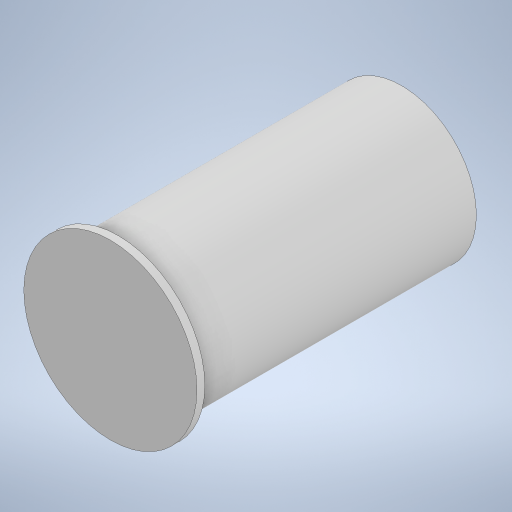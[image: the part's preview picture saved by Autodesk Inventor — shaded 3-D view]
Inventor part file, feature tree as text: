
AUTODESK INVENTOR PART (.ipt)
format: ipt  version: 2024.2 (Build 282272000, 272)  size: 210,944 bytes
history: native  units: mm
features: extrude x2, sketch x2
ambient origin geometry x8: Origin, YZ Plane, XZ Plane, XY Plane, X Axis, Y Axis, Z Axis, Center Point
bodies: Solid1 (feature_tree)
feature tree (4):
  extrude  "Extrusion1"  Depth=18.0mm TaperAngle=0.0deg
  extrude  "Extrusion2"  Depth=0.5mm TaperAngle=0.0deg
  sketch  "Sketch1"  dims[d0=9.5mm d2=18.0mm d3=0.0mm]
  sketch  "Sketch2"  dims[d4=11.0mm d5=0.5mm d6=0.0mm]
